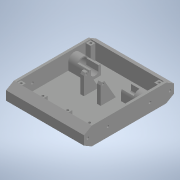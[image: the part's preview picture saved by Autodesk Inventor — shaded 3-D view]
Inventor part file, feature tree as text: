
AUTODESK INVENTOR PART (.ipt)
format: ipt  version: 2020 (Build 240168000, 168)  size: 390,144 bytes
history: native  units: in
note: dims shown in document units (in); Inventor stores cm internally (conversion verified against a paired STEP export)
features: projected_geometry x13, extrude x11, sketch x11, mirror x4, plane x1
ambient origin geometry x8: Origin, YZ Plane, XZ Plane, XY Plane, X Axis, Y Axis, Z Axis, Center Point
bodies: Solid1 (feature_tree)
feature tree (40):
  extrude  "Extrusion1"  Depth=5.9055in
  extrude  "Extrusion2"  TaperAngle=0.0deg  [1 undecoded]
  extrude  "Extrusion3"  Depth=1.063in
  extrude  "Extrusion4"  Depth=0.315in
  extrude  "Extrusion5"  TaperAngle=0.0deg  [1 undecoded]
  extrude  "Extrusion6"  Depth=0.5906in
  mirror  "Mirror1"
  extrude  "Extrusion7"  Depth=0.0787in
  mirror  "Mirror2"
  extrude  "Extrusion8"  Depth=0.5512in
  mirror  "Mirror3"
  plane  "Work Plane1"
  extrude  "Extrusion9"  Depth=0.7874in TaperAngle=0.0deg
  mirror  "Mirror4"
  extrude  "Extrusion10"  Depth=6.063in TaperAngle=0.0deg
  extrude  "Extrusion11"  Depth=0.1575in
  sketch  "Sketch1"  dims[d0=1.1811in d1=5.9055in]
  sketch  "Sketch2"  dims[d2=5.1181in d3=0.0in]
  projected_geometry  "Projected Loop1"
  sketch  "Sketch3"  dims[d4=0.1575in d5=1.063in]
  projected_geometry  "Projected Loop2"
  projected_geometry  "Projected Loop3"
  sketch  "Sketch4"  dims[d6=0.0in d8=0.315in]
  sketch  "Sketch5"  dims[d10=0.993in d11=0.0in]
  projected_geometry  "Projected Loop4"
  sketch  "Sketch6"  dims[d12=0.6496in d13=0.5906in]
  sketch  "Sketch7"  dims[d14=1.5748in d15=0.0787in]
  sketch  "Sketch9"  dims[d16=0.5512in d17=0.0in d18=0.6102in]
  sketch  "Sketch10"  dims[d19=0.4803in d20=0.7874in d21=0.0in]
  sketch  "Sketch12"  dims[d22=0.1654in d23=6.063in d24=0.0in]
  projected_geometry  "Projected Loop6"
  projected_geometry  "Projected Loop7"
  projected_geometry  "Projected Loop8"
  sketch  "Sketch13"  dims[d25=0.5114in d26=0.1575in d27=1.5748in d28=0.0in d29=0.0in d30=0.1575in d31=0.2756in d32=0.0in d33=0.4331in d34=0.122in d38=2.7559in d40=0.061in d41=0.0909in d42=0.2362in d43=0.0in d44=60.0deg d45=0.0787in d46=0.315in d48=0.993in d49=0.0in d51=0.1575in d52=0.1575in d53=0.2756in d54=0.0in d55=0.6543in]
  projected_geometry  "Projected Loop9"
  projected_geometry  "Projected Loop10"
  projected_geometry  "Projected Loop11"
  projected_geometry  "Projected Loop12"
  projected_geometry  "Projected Loop13"
  projected_geometry  "Projected Loop14"
note: 2 required parameter values undecoded (feature->parameter linkage not recoverable at this tier; creation-order binding heuristic only, values carry confidence <= 0.55)
